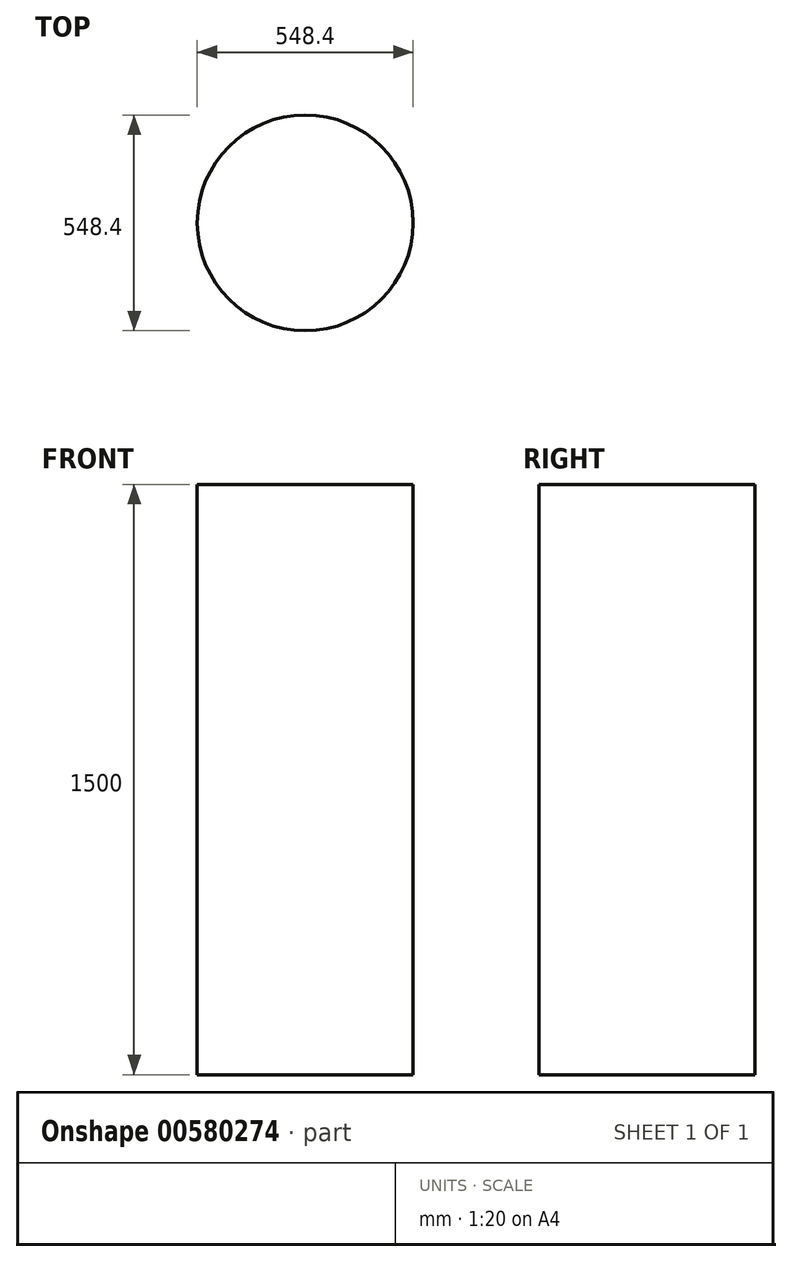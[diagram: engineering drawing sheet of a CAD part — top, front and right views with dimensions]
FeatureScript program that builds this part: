
annotation { "Feature Type Name" : "Feature", "Feature Type Description" : "" }
export const myFeature = defineFeature(function(context is Context, id is Id, definition is map)
    precondition{}
    {
        {
            var Q0;
            Q0=qCreatedBy(makeId("Top.planeOp"),FACE);
            var sketch = newSketch(context, id + "F0", { "sketchPlane" : qUnion([Q0])});
            skCircle(sketch, "E0", {"center": v(0, 0) * mm, "radius": 274.2 * mm});
            skSolve(sketch);
        }
        {
            var Q0;
            Q0 = qSketchRegion(id + "F0", true);
            extrude(context, id + "F1", {"entities" : qUnion([Q0]), "depth" : 1500 * mm, "offsetDistance" : 25 * mm});
        }
    });
